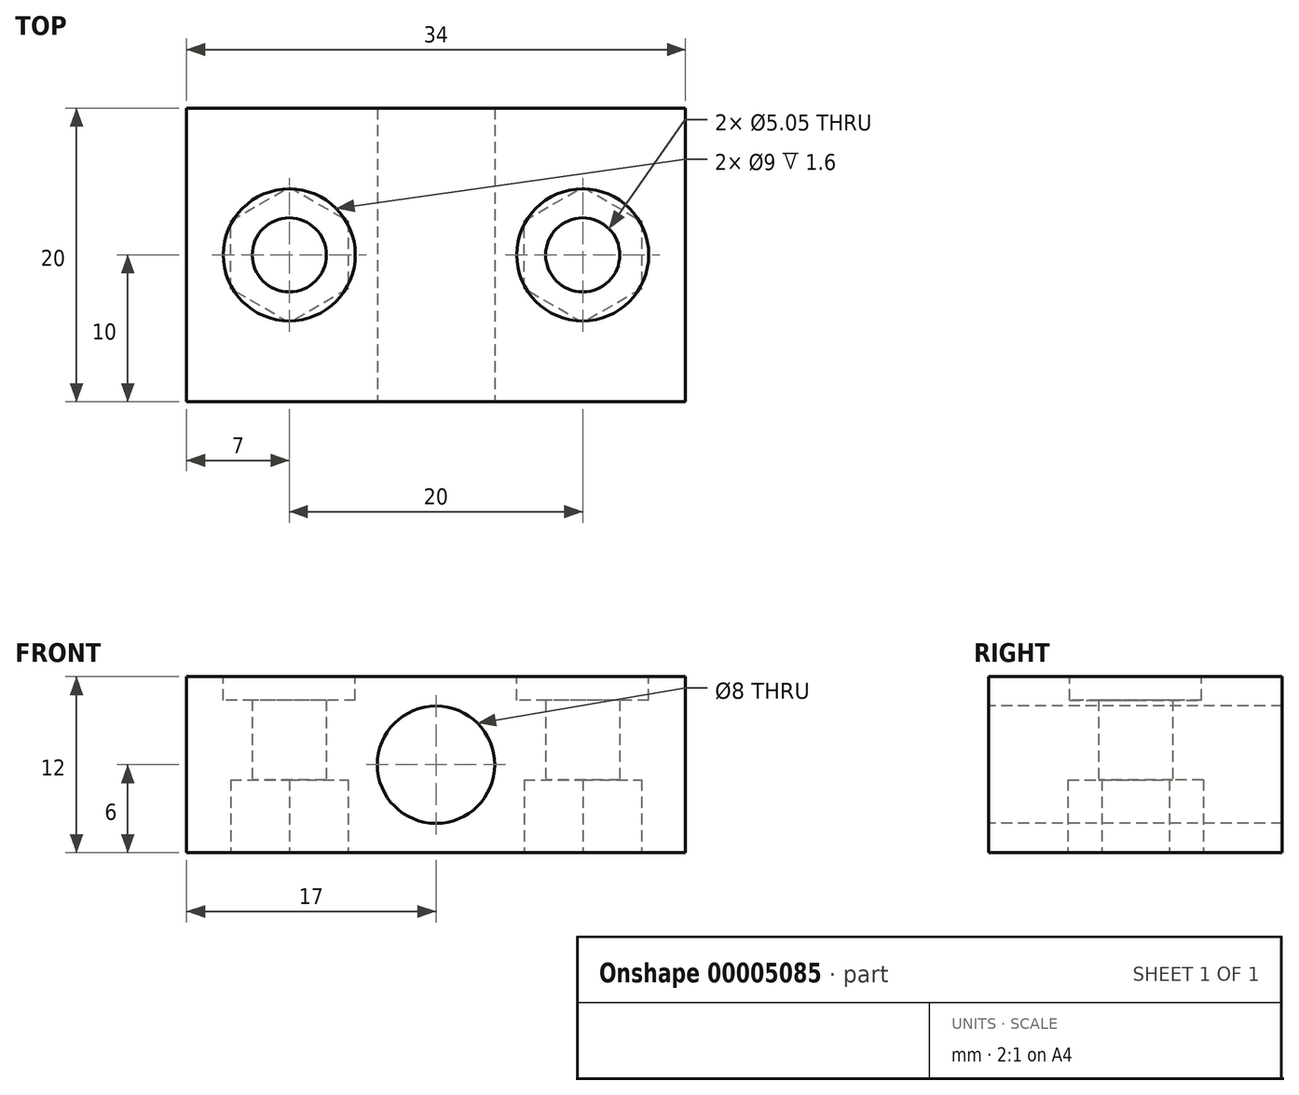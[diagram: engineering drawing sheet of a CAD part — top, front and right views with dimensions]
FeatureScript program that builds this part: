
annotation { "Feature Type Name" : "Feature", "Feature Type Description" : "" }
export const myFeature = defineFeature(function(context is Context, id is Id, definition is map)
    precondition{}
    {
        {
            var Q0;
            Q0=qCreatedBy(makeId("Top.planeOp"),FACE);
            var sketch = newSketch(context, id + "F0", { "sketchPlane" : qUnion([Q0])});
            skLineSegment(sketch, "E0.bottom", {"start": v(-17, 0) * mm, "end": v(17, 0) * mm});
            skLineSegment(sketch, "E0.top", {"start": v(-17, 20) * mm, "end": v(17, 20) * mm});
            skLineSegment(sketch, "E0.left", {"start": v(-17, 0) * mm, "end": v(-17, 20) * mm});
            skLineSegment(sketch, "E0.right", {"start": v(17, 0) * mm, "end": v(17, 20) * mm});
            skCircle(sketch, "E1", {"center": v(-10, 10) * mm, "radius": 2.52 * mm});
            skCircle(sketch, "E2", {"center": v(10, 10) * mm, "radius": 2.52 * mm});
            skSolve(sketch);
        }
        {
            var Q0;
            Q0=makeQuery(id+"F0.imprint","IMPRINT",FACE,{"disambiguationData":[TD([[makeQuery(id+"F0.imprint","IMPRINT",EDGE,{"derivedFrom":sQuery(id+"F0.wireOp",EDGE,"E0.bottom")}),1.0]])]});
            extrude(context, id + "F1", {"entities" : qUnion([Q0]), "depth" : 12 * mm});
        }
        {
            var Q0;
            Q0=makeQuery(id+"F1.opExtrude","SWEPT_FACE",FACE,{"disambiguationData":[OSD([sQuery(id+"F0.wireOp",EDGE,"E0.bottom")])]});
            var sketch = newSketch(context, id + "F2", { "sketchPlane" : qUnion([Q0])});
            skCircle(sketch, "E3", {"center": v(0, 6) * mm, "radius": 4 * mm});
            skSolve(sketch);
        }
        {
            var Q0;
            Q0=makeQuery(id+"F2.imprint","IMPRINT",FACE,{"disambiguationData":[TD([[makeQuery(id+"F2.imprint","IMPRINT",EDGE,{"derivedFrom":sQuery(id+"F2.wireOp",EDGE,"E3")}),1.0]])]});
            extrude(context, id + "F3", {"entities" : qUnion([Q0]), "operationType" : NewBodyOperationType.REMOVE, "endBound" : BoundingType.UP_TO_NEXT, "oppositeDirection" : true, "depth" : 25 * mm});
        }
        {
            var Q0;
            Q0=makeQuery(id+"F0.imprint","IMPRINT",FACE,{"disambiguationData":[TD([[makeQuery(id+"F0.imprint","IMPRINT",EDGE,{"derivedFrom":sQuery(id+"F0.wireOp",EDGE,"E0.bottom")}),1.0]])]});
            var sketch = newSketch(context, id + "F4", { "sketchPlane" : qUnion([Q0])});
            skCircle(sketch, "E4.cCircle", {"center": v(-10, 10) * mm, "radius": 4.62 * mm, "construction": true});
            skLineSegment(sketch, "E4.0", {"start": v(-10, 14.62) * mm, "end": v(-6, 12.3) * mm});
            skLineSegment(sketch, "E4.1", {"start": v(-6, 12.3) * mm, "end": v(-6, 7.69) * mm});
            skLineSegment(sketch, "E4.2", {"start": v(-6, 7.69) * mm, "end": v(-10, 5.38) * mm});
            skLineSegment(sketch, "E4.3", {"start": v(-10, 5.38) * mm, "end": v(-14, 7.7) * mm});
            skLineSegment(sketch, "E4.4", {"start": v(-14, 7.7) * mm, "end": v(-14, 12.31) * mm});
            skLineSegment(sketch, "E4.5", {"start": v(-14, 12.31) * mm, "end": v(-10, 14.62) * mm});
            skCircle(sketch, "E5.cCircle", {"center": v(10, 10) * mm, "radius": 4.62 * mm, "construction": true});
            skLineSegment(sketch, "E5.0", {"start": v(10, 14.62) * mm, "end": v(14, 12.31) * mm});
            skLineSegment(sketch, "E5.1", {"start": v(14, 12.31) * mm, "end": v(14, 7.7) * mm});
            skLineSegment(sketch, "E5.2", {"start": v(14, 7.7) * mm, "end": v(10, 5.38) * mm});
            skLineSegment(sketch, "E5.3", {"start": v(10, 5.38) * mm, "end": v(6, 7.7) * mm});
            skLineSegment(sketch, "E5.4", {"start": v(6, 7.7) * mm, "end": v(6, 12.31) * mm});
            skLineSegment(sketch, "E5.5", {"start": v(6, 12.31) * mm, "end": v(10, 14.62) * mm});
            skSolve(sketch);
        }
        {
            var Q0;
            Q0=qSketchRegion(id+"F4",true);
            extrude(context, id + "F5", {"entities" : qUnion([Q0]), "operationType" : NewBodyOperationType.REMOVE, "depth" : 4.97 * mm});
        }
        {
            var Q0;
            Q0=makeQuery(id+"F1.opExtrude","CAP_FACE",FACE,{"disambiguationData":[OSD([sQuery(id+"F0.wireOp",EDGE,"E0.bottom"),sQuery(id+"F0.wireOp",EDGE,"E0.top"),sQuery(id+"F0.wireOp",EDGE,"E0.left"),sQuery(id+"F0.wireOp",EDGE,"E0.right"),sQuery(id+"F0.wireOp",EDGE,"E1"),sQuery(id+"F0.wireOp",EDGE,"E2")])],"isStart":false});
            var sketch = newSketch(context, id + "F6", { "sketchPlane" : qUnion([Q0])});
            skCircle(sketch, "E6", {"center": v(-10, 10) * mm, "radius": 4.5 * mm});
            skCircle(sketch, "E7", {"center": v(10, 10) * mm, "radius": 4.5 * mm});
            skSolve(sketch);
        }
        {
            var Q0;
            Q0=makeQuery(id+"F6.imprint","IMPRINT",FACE,{"disambiguationData":[TD([[makeQuery(id+"F6.imprint","IMPRINT",EDGE,{"derivedFrom":sQuery(id+"F6.wireOp",EDGE,"E6")}),1.0]])]});
            var Q1;
            Q1=makeQuery(id+"F6.imprint","IMPRINT",FACE,{"disambiguationData":[TD([[makeQuery(id+"F6.imprint","IMPRINT",EDGE,{"derivedFrom":sQuery(id+"F6.wireOp",EDGE,"E7")}),1.0]])]});
            extrude(context, id + "F7", {"entities" : qUnion([Q0, Q1]), "operationType" : NewBodyOperationType.REMOVE, "oppositeDirection" : true, "depth" : 1.6 * mm});
        }
    });
